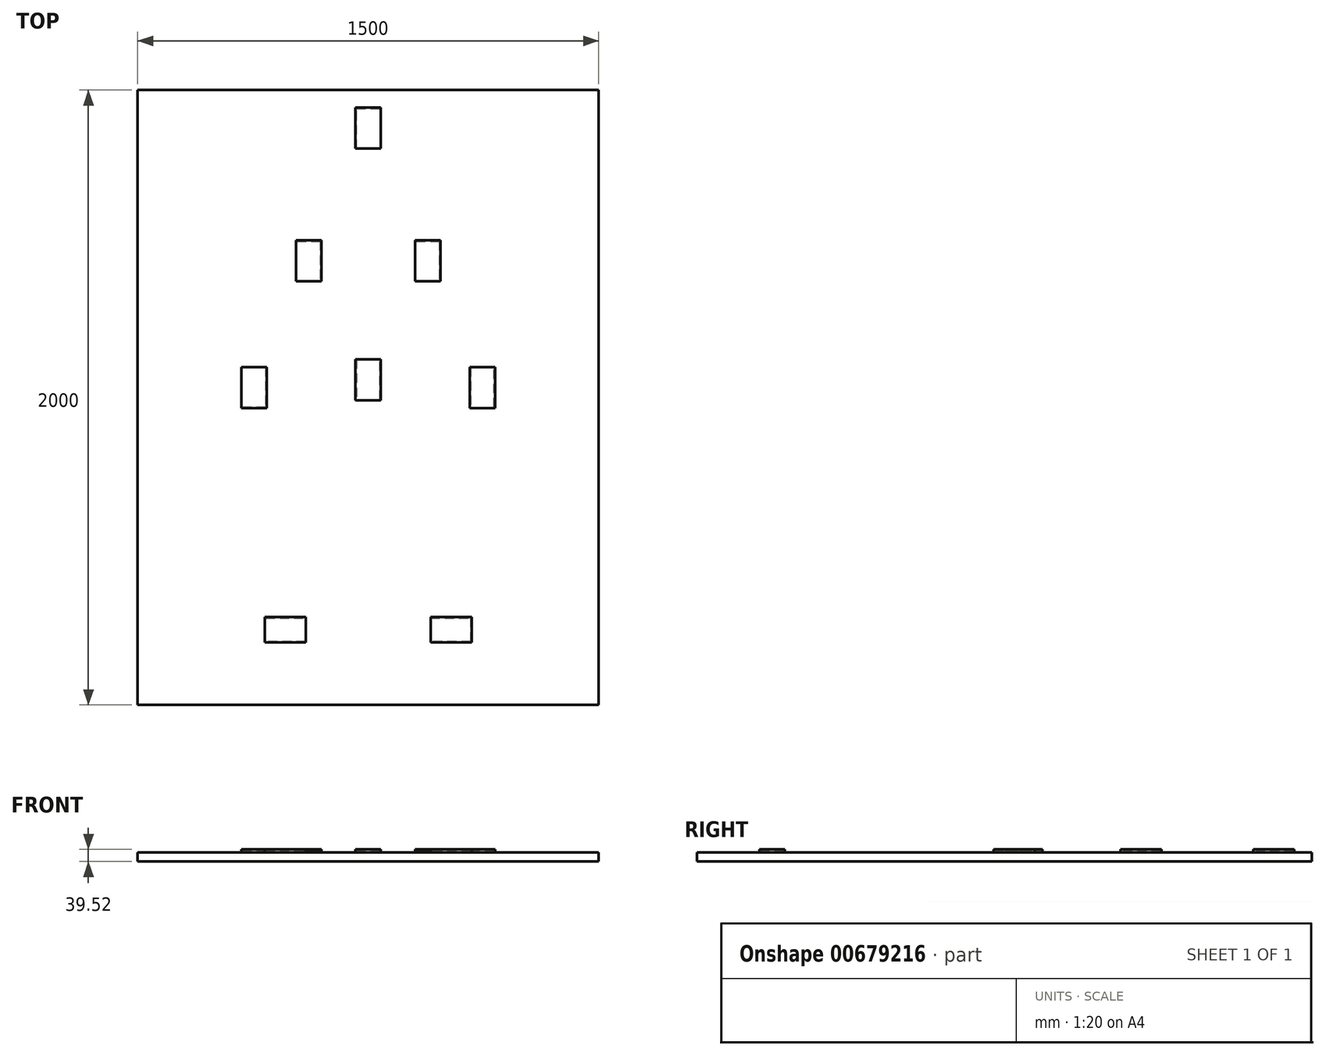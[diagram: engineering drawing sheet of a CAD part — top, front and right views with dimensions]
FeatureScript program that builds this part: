
annotation { "Feature Type Name" : "Feature", "Feature Type Description" : "" }
export const myFeature = defineFeature(function(context is Context, id is Id, definition is map)
    precondition{}
    {
        {
            var Q0;
            Q0=qCreatedBy(makeId("Top.planeOp"),FACE);
            var sketch = newSketch(context, id + "F0", { "sketchPlane" : qUnion([Q0])});
            skLineSegment(sketch, "E0.bottom", {"start": v(0, 0) * mm, "end": v(1500, 0) * mm});
            skLineSegment(sketch, "E0.top", {"start": v(0, 2000) * mm, "end": v(1500, 2000) * mm});
            skLineSegment(sketch, "E0.left", {"start": v(0, 0) * mm, "end": v(0, 2000) * mm});
            skLineSegment(sketch, "E0.right", {"start": v(1500, 0) * mm, "end": v(1500, 2000) * mm});
            skSolve(sketch);
        }
        {
            var Q0;
            Q0=makeQuery(id+"F0.imprint","IMPRINT",FACE,{"disambiguationData":[TD([[makeQuery(id+"F0.imprint","IMPRINT",EDGE,{"derivedFrom":sQuery(id+"F0.wireOp",EDGE,"E0.bottom")}),1.0]])]});
            extrude(context, id + "F1", {"entities" : qUnion([Q0]), "depth" : 5 * mm, "offsetDistance" : 25 * mm});
        }
        {
            var Q0;
            Q0=makeQuery(id+"F1.opExtrude","CAP_FACE",FACE,{"disambiguationData":[OSD([sQuery(id+"F0.wireOp",EDGE,"E0.bottom"),sQuery(id+"F0.wireOp",EDGE,"E0.top"),sQuery(id+"F0.wireOp",EDGE,"E0.left"),sQuery(id+"F0.wireOp",EDGE,"E0.right")])],"isStart":false});
            var sketch = newSketch(context, id + "F2", { "sketchPlane" : qUnion([Q0])});
            skLineSegment(sketch, "E1", {"start": v(0, 0) * mm, "end": v(10, 0) * mm});
            skLineSegment(sketch, "E2", {"start": v(10, 0) * mm, "end": v(10, 10) * mm});
            skLineSegment(sketch, "E3", {"start": v(1500, 2000) * mm, "end": v(1500, 1990) * mm});
            skLineSegment(sketch, "E4", {"start": v(1500, 1990) * mm, "end": v(1490, 1990) * mm});
            skLineSegment(sketch, "E5.bottom", {"start": v(1490, 1990) * mm, "end": v(10, 1990) * mm});
            skLineSegment(sketch, "E5.top", {"start": v(1490, 10) * mm, "end": v(10, 10) * mm});
            skLineSegment(sketch, "E5.left", {"start": v(1490, 1990) * mm, "end": v(1490, 10) * mm});
            skLineSegment(sketch, "E5.right", {"start": v(10, 1990) * mm, "end": v(10, 10) * mm});
            skSolve(sketch);
        }
        {
            var Q0;
            Q0=qSketchRegion(id+"F2",true);
            extrude(context, id + "F3", {"entities" : qUnion([Q0]), "depth" : 20 * mm, "offsetDistance" : 25 * mm});
        }
        {
            var Q0;
            Q0=makeQuery(id+"F2.imprint","IMPRINT",FACE,{"disambiguationData":[TD([[makeQuery(id+"F2.imprint","IMPRINT",EDGE,{"derivedFrom":sQuery(id+"F2.wireOp",EDGE,"E1")}),1.0]])]});
            var Q1;
            {var subQ1=sQuery(id+"F2.wireOp",EDGE,"E2");Q1=makeQuery(id+"F2.imprint","IMPRINT",FACE,{"disambiguationData":[TD([[makeQuery(id+"F2.imprint","IMPRINT",EDGE,{"derivedFrom":subQ1}),-1.0]])]});}
            extrude(context, id + "F4", {"entities" : qUnion([Q0, Q1]), "operationType" : NewBodyOperationType.ADD, "depth" : 20 * mm, "offsetDistance" : 25 * mm});
        }
        {
            var Q0;
            Q0=makeQuery(id+"F4.opExtrude","CAP_FACE",FACE,{"disambiguationData":[OSD([sQuery(id+"F0.wireOp",EDGE,"E0.bottom"),sQuery(id+"F0.wireOp",EDGE,"E0.top"),sQuery(id+"F0.wireOp",EDGE,"E0.left"),sQuery(id+"F0.wireOp",EDGE,"E0.right"),sQuery(id+"F2.wireOp",EDGE,"E1"),sQuery(id+"F2.wireOp",EDGE,"E3"),sQuery(id+"F2.wireOp",EDGE,"E5.bottom"),sQuery(id+"F2.wireOp",EDGE,"E5.top"),sQuery(id+"F2.wireOp",EDGE,"E5.left"),sQuery(id+"F2.wireOp",EDGE,"E5.right")])],"isStart":false});
            var sketch = newSketch(context, id + "F5", { "sketchPlane" : qUnion([Q0])});
            skLineSegment(sketch, "E6.bottom", {"start": v(0, 0) * mm, "end": v(1500, 0) * mm});
            skLineSegment(sketch, "E6.top", {"start": v(0, 2000) * mm, "end": v(1500, 2000) * mm});
            skLineSegment(sketch, "E6.left", {"start": v(0, 0) * mm, "end": v(0, 2000) * mm});
            skLineSegment(sketch, "E6.right", {"start": v(1500, 0) * mm, "end": v(1500, 2000) * mm});
            skSolve(sketch);
        }
        {
            var Q0;
            Q0=qSketchRegion(id+"F5",true);
            extrude(context, id + "F6", {"entities" : qUnion([Q0]), "operationType" : NewBodyOperationType.ADD, "depth" : 5 * mm, "offsetDistance" : 25 * mm});
        }
        {
            var Q0;
            Q0=makeQuery(id+"F6.opExtrude","CAP_FACE",FACE,{"disambiguationData":[OSD([sQuery(id+"F5.wireOp",EDGE,"E6.bottom"),sQuery(id+"F5.wireOp",EDGE,"E6.top"),sQuery(id+"F5.wireOp",EDGE,"E6.left"),sQuery(id+"F5.wireOp",EDGE,"E6.right")])],"isStart":false});
            var sketch = newSketch(context, id + "F7", { "sketchPlane" : qUnion([Q0])});
            skLineSegment(sketch, "E7", {"start": v(750, 0) * mm, "end": v(750, 203.2) * mm});
            skLineSegment(sketch, "E8", {"start": v(750, 203.2) * mm, "end": v(546.8, 203.2) * mm});
            skLineSegment(sketch, "E9", {"start": v(750, 203.2) * mm, "end": v(953.2, 203.2) * mm});
            skLineSegment(sketch, "E10", {"start": v(750, 203.2) * mm, "end": v(750, 990.6) * mm});
            skLineSegment(sketch, "E11", {"start": v(750, 990.6) * mm, "end": v(1080.2, 990.6) * mm});
            skLineSegment(sketch, "E12", {"start": v(750, 990.6) * mm, "end": v(419.8, 990.6) * mm});
            skLineSegment(sketch, "E13", {"start": v(419.8, 990.6) * mm, "end": v(419.8, 965.2) * mm});
            skLineSegment(sketch, "E14", {"start": v(1080.2, 990.6) * mm, "end": v(1080.2, 965.2) * mm});
            skLineSegment(sketch, "E15", {"start": v(750, 990.6) * mm, "end": v(750, 1377.95) * mm});
            skLineSegment(sketch, "E16", {"start": v(750, 1377.95) * mm, "end": v(902.4, 1377.95) * mm});
            skLineSegment(sketch, "E17", {"start": v(750, 1377.95) * mm, "end": v(597.6, 1377.95) * mm});
            skLineSegment(sketch, "E18", {"start": v(750, 1377.95) * mm, "end": v(750, 1809.75) * mm});
            skLineSegment(sketch, "E19.bottom", {"start": v(419.8, 965.2) * mm, "end": v(337.25, 965.2) * mm});
            skLineSegment(sketch, "E19.left", {"start": v(419.8, 965.2) * mm, "end": v(419.8, 1098.55) * mm});
            skLineSegment(sketch, "E19.right", {"start": v(337.25, 965.2) * mm, "end": v(337.25, 1098.55) * mm});
            skLineSegment(sketch, "E20.bottom", {"start": v(1080.2, 965.2) * mm, "end": v(1162.75, 965.2) * mm});
            skLineSegment(sketch, "E20.left", {"start": v(1080.2, 965.2) * mm, "end": v(1080.2, 1098.55) * mm});
            skLineSegment(sketch, "E20.right", {"start": v(1162.75, 965.2) * mm, "end": v(1162.75, 1098.55) * mm});
            skLineSegment(sketch, "E21.top", {"start": v(902.4, 1511.3) * mm, "end": v(984.95, 1511.3) * mm});
            skLineSegment(sketch, "E21.left", {"start": v(902.4, 1377.95) * mm, "end": v(902.4, 1511.3) * mm});
            skLineSegment(sketch, "E21.right", {"start": v(984.95, 1377.95) * mm, "end": v(984.95, 1511.3) * mm});
            skLineSegment(sketch, "E22.top", {"start": v(597.6, 1511.3) * mm, "end": v(515.05, 1511.3) * mm});
            skLineSegment(sketch, "E22.left", {"start": v(597.6, 1377.95) * mm, "end": v(597.6, 1511.3) * mm});
            skLineSegment(sketch, "E22.right", {"start": v(515.05, 1377.95) * mm, "end": v(515.05, 1511.3) * mm});
            skLineSegment(sketch, "E23", {"start": v(750, 1809.75) * mm, "end": v(708.73, 1809.75) * mm});
            skLineSegment(sketch, "E24.top", {"start": v(708.73, 1943.1) * mm, "end": v(791.28, 1943.1) * mm});
            skLineSegment(sketch, "E24.left", {"start": v(708.73, 1809.75) * mm, "end": v(708.73, 1943.1) * mm});
            skLineSegment(sketch, "E24.right", {"start": v(791.28, 1809.75) * mm, "end": v(791.28, 1943.1) * mm});
            skLineSegment(sketch, "E25.bottom", {"start": v(953.2, 203.2) * mm, "end": v(1086.55, 203.2) * mm});
            skLineSegment(sketch, "E25.top", {"start": v(953.2, 285.75) * mm, "end": v(1086.55, 285.75) * mm});
            skLineSegment(sketch, "E25.right", {"start": v(1086.55, 203.2) * mm, "end": v(1086.55, 285.75) * mm});
            skLineSegment(sketch, "E26.bottom", {"start": v(546.8, 203.2) * mm, "end": v(413.45, 203.2) * mm});
            skLineSegment(sketch, "E26.top", {"start": v(546.8, 285.75) * mm, "end": v(413.45, 285.75) * mm});
            skLineSegment(sketch, "E26.right", {"start": v(413.45, 203.2) * mm, "end": v(413.45, 285.75) * mm});
            skLineSegment(sketch, "E27", {"start": v(515.05, 1377.95) * mm, "end": v(518.23, 1377.95) * mm});
            skLineSegment(sketch, "E28", {"start": v(518.23, 1377.95) * mm, "end": v(518.23, 1508.13) * mm});
            skLineSegment(sketch, "E29", {"start": v(518.23, 1508.13) * mm, "end": v(594.43, 1508.13) * mm});
            skLineSegment(sketch, "E30", {"start": v(594.43, 1508.13) * mm, "end": v(594.43, 1377.95) * mm});
            skLineSegment(sketch, "E31", {"start": v(594.43, 1377.95) * mm, "end": v(597.6, 1377.95) * mm});
            skLineSegment(sketch, "E32", {"start": v(902.4, 1377.95) * mm, "end": v(905.58, 1377.95) * mm});
            skLineSegment(sketch, "E33", {"start": v(905.58, 1377.95) * mm, "end": v(905.58, 1508.13) * mm});
            skLineSegment(sketch, "E34", {"start": v(905.58, 1508.13) * mm, "end": v(981.78, 1508.13) * mm});
            skLineSegment(sketch, "E35", {"start": v(981.78, 1508.13) * mm, "end": v(981.78, 1377.95) * mm});
            skLineSegment(sketch, "E36", {"start": v(981.78, 1377.95) * mm, "end": v(984.95, 1377.95) * mm});
            skLineSegment(sketch, "E37", {"start": v(708.73, 1809.75) * mm, "end": v(711.9, 1809.75) * mm});
            skLineSegment(sketch, "E38", {"start": v(711.9, 1809.75) * mm, "end": v(711.9, 1939.93) * mm});
            skLineSegment(sketch, "E39", {"start": v(711.9, 1939.93) * mm, "end": v(788.1, 1939.93) * mm});
            skLineSegment(sketch, "E40", {"start": v(788.1, 1939.93) * mm, "end": v(788.1, 1809.75) * mm});
            skLineSegment(sketch, "E41", {"start": v(788.1, 1809.75) * mm, "end": v(791.28, 1809.75) * mm});
            skLineSegment(sketch, "E42", {"start": v(419.8, 1098.55) * mm, "end": v(416.62, 1098.55) * mm});
            skLineSegment(sketch, "E43", {"start": v(416.62, 1098.55) * mm, "end": v(416.62, 968.38) * mm});
            skLineSegment(sketch, "E44", {"start": v(416.62, 968.38) * mm, "end": v(340.42, 968.38) * mm});
            skLineSegment(sketch, "E45", {"start": v(340.42, 968.38) * mm, "end": v(340.42, 1098.55) * mm});
            skLineSegment(sketch, "E46", {"start": v(340.42, 1098.55) * mm, "end": v(337.25, 1098.55) * mm});
            skLineSegment(sketch, "E47", {"start": v(1080.2, 1098.55) * mm, "end": v(1083.38, 1098.55) * mm});
            skLineSegment(sketch, "E48", {"start": v(1083.38, 1098.55) * mm, "end": v(1083.38, 968.38) * mm});
            skLineSegment(sketch, "E49", {"start": v(1083.38, 968.38) * mm, "end": v(1159.58, 968.38) * mm});
            skLineSegment(sketch, "E50", {"start": v(1159.58, 968.38) * mm, "end": v(1159.58, 1098.55) * mm});
            skLineSegment(sketch, "E51", {"start": v(1159.58, 1098.55) * mm, "end": v(1162.75, 1098.55) * mm});
            skLineSegment(sketch, "E52", {"start": v(546.8, 203.2) * mm, "end": v(546.8, 206.38) * mm});
            skLineSegment(sketch, "E53", {"start": v(546.8, 206.38) * mm, "end": v(416.62, 206.38) * mm});
            skLineSegment(sketch, "E54", {"start": v(416.62, 206.38) * mm, "end": v(416.62, 282.58) * mm});
            skLineSegment(sketch, "E55", {"start": v(416.62, 282.58) * mm, "end": v(546.8, 282.58) * mm});
            skLineSegment(sketch, "E56", {"start": v(546.8, 282.58) * mm, "end": v(546.8, 285.75) * mm});
            skLineSegment(sketch, "E57", {"start": v(953.2, 285.75) * mm, "end": v(953.2, 282.58) * mm});
            skLineSegment(sketch, "E58", {"start": v(953.2, 282.58) * mm, "end": v(1083.38, 282.58) * mm});
            skLineSegment(sketch, "E59", {"start": v(1083.38, 282.58) * mm, "end": v(1083.38, 206.38) * mm});
            skLineSegment(sketch, "E60", {"start": v(1083.38, 206.38) * mm, "end": v(953.2, 206.38) * mm});
            skLineSegment(sketch, "E61", {"start": v(953.2, 206.38) * mm, "end": v(953.2, 203.2) * mm});
            skLineSegment(sketch, "E62", {"start": v(1162.75, 1098.55) * mm, "end": v(1080.2, 1098.55) * mm});
            skLineSegment(sketch, "E63", {"start": v(984.95, 1377.95) * mm, "end": v(902.4, 1377.95) * mm});
            skLineSegment(sketch, "E64", {"start": v(597.6, 1377.95) * mm, "end": v(515.05, 1377.95) * mm});
            skLineSegment(sketch, "E65", {"start": v(419.8, 1098.55) * mm, "end": v(337.25, 1098.55) * mm});
            skLineSegment(sketch, "E66", {"start": v(791.28, 1809.75) * mm, "end": v(708.73, 1809.75) * mm});
            skLineSegment(sketch, "E67", {"start": v(953.2, 203.2) * mm, "end": v(953.2, 285.75) * mm});
            skLineSegment(sketch, "E68", {"start": v(546.8, 203.2) * mm, "end": v(546.8, 285.75) * mm});
            skLineSegment(sketch, "E69", {"start": v(750, 990.6) * mm, "end": v(708.73, 990.6) * mm});
            skLineSegment(sketch, "E70.bottom", {"start": v(708.73, 990.6) * mm, "end": v(791.28, 990.6) * mm});
            skLineSegment(sketch, "E70.top", {"start": v(708.73, 1123.95) * mm, "end": v(791.28, 1123.95) * mm});
            skLineSegment(sketch, "E70.left", {"start": v(708.73, 990.6) * mm, "end": v(708.73, 1123.95) * mm});
            skLineSegment(sketch, "E70.right", {"start": v(791.28, 990.6) * mm, "end": v(791.28, 1123.95) * mm});
            skLineSegment(sketch, "E71", {"start": v(708.73, 1123.95) * mm, "end": v(711.9, 1123.95) * mm});
            skLineSegment(sketch, "E72", {"start": v(711.9, 1123.95) * mm, "end": v(711.9, 993.78) * mm});
            skLineSegment(sketch, "E73", {"start": v(711.9, 993.78) * mm, "end": v(788.1, 993.78) * mm});
            skLineSegment(sketch, "E74", {"start": v(788.1, 993.78) * mm, "end": v(788.1, 1123.95) * mm});
            skSolve(sketch);
        }
        {
            var Q0;
            Q0=makeQuery(id+"F7.imprint","IMPRINT",FACE,{"disambiguationData":[TD([[makeQuery(id+"F7.imprint","IMPRINT",EDGE,{"derivedFrom":sQuery(id+"F7.wireOp",EDGE,"E22.top")}),1.0]])]});
            var Q1;
            {var subQ0=sQuery(id+"F7.wireOp",EDGE,"E28");Q1=makeQuery(id+"F7.imprint","IMPRINT",FACE,{"disambiguationData":[TD([[makeQuery(id+"F7.imprint","IMPRINT",EDGE,{"derivedFrom":subQ0}),-1.0]])]});}
            var Q2;
            {var subQ0=sQuery(id+"F7.wireOp",EDGE,"E33");Q2=makeQuery(id+"F7.imprint","IMPRINT",FACE,{"disambiguationData":[TD([[makeQuery(id+"F7.imprint","IMPRINT",EDGE,{"derivedFrom":subQ0}),-1.0]])]});}
            var Q3;
            Q3=makeQuery(id+"F7.imprint","IMPRINT",FACE,{"disambiguationData":[TD([[makeQuery(id+"F7.imprint","IMPRINT",EDGE,{"derivedFrom":sQuery(id+"F7.wireOp",EDGE,"E21.top")}),-1.0]])]});
            var Q4;
            Q4=makeQuery(id+"F7.imprint","IMPRINT",FACE,{"disambiguationData":[TD([[makeQuery(id+"F7.imprint","IMPRINT",EDGE,{"derivedFrom":sQuery(id+"F7.wireOp",EDGE,"E24.top")}),-1.0]])]});
            var Q5;
            {var subQ3=sQuery(id+"F7.wireOp",EDGE,"E38");Q5=makeQuery(id+"F7.imprint","IMPRINT",FACE,{"disambiguationData":[TD([[makeQuery(id+"F7.imprint","IMPRINT",EDGE,{"derivedFrom":subQ3}),-1.0]])]});}
            var Q6;
            {var subQ5=sQuery(id+"F7.wireOp",EDGE,"E19.bottom");Q6=makeQuery(id+"F7.imprint","IMPRINT",FACE,{"disambiguationData":[TD([[makeQuery(id+"F7.imprint","IMPRINT",EDGE,{"derivedFrom":subQ5}),-1.0]])]});}
            var Q7;
            {var subQ0=sQuery(id+"F7.wireOp",EDGE,"E43");Q7=makeQuery(id+"F7.imprint","IMPRINT",FACE,{"disambiguationData":[TD([[makeQuery(id+"F7.imprint","IMPRINT",EDGE,{"derivedFrom":subQ0}),-1.0]])]});}
            var Q8;
            {var subQ0=sQuery(id+"F7.wireOp",EDGE,"E53");Q8=makeQuery(id+"F7.imprint","IMPRINT",FACE,{"disambiguationData":[TD([[makeQuery(id+"F7.imprint","IMPRINT",EDGE,{"derivedFrom":subQ0}),-1.0]])]});}
            var Q9;
            {var subQ4=sQuery(id+"F7.wireOp",EDGE,"E26.bottom");Q9=makeQuery(id+"F7.imprint","IMPRINT",FACE,{"disambiguationData":[TD([[makeQuery(id+"F7.imprint","IMPRINT",EDGE,{"derivedFrom":subQ4}),-1.0]])]});}
            var Q10;
            {var subQ0=sQuery(id+"F7.wireOp",EDGE,"E58");Q10=makeQuery(id+"F7.imprint","IMPRINT",FACE,{"disambiguationData":[TD([[makeQuery(id+"F7.imprint","IMPRINT",EDGE,{"derivedFrom":subQ0}),-1.0]])]});}
            var Q11;
            {var subQ3=sQuery(id+"F7.wireOp",EDGE,"E25.bottom");Q11=makeQuery(id+"F7.imprint","IMPRINT",FACE,{"disambiguationData":[TD([[makeQuery(id+"F7.imprint","IMPRINT",EDGE,{"derivedFrom":subQ3}),1.0]])]});}
            var Q12;
            {var subQ5=sQuery(id+"F7.wireOp",EDGE,"E20.bottom");Q12=makeQuery(id+"F7.imprint","IMPRINT",FACE,{"disambiguationData":[TD([[makeQuery(id+"F7.imprint","IMPRINT",EDGE,{"derivedFrom":subQ5}),1.0]])]});}
            var Q13;
            {var subQ0=sQuery(id+"F7.wireOp",EDGE,"E48");Q13=makeQuery(id+"F7.imprint","IMPRINT",FACE,{"disambiguationData":[TD([[makeQuery(id+"F7.imprint","IMPRINT",EDGE,{"derivedFrom":subQ0}),1.0]])]});}
            var Q14;
            {var subQ5=sQuery(id+"F7.wireOp",EDGE,"E72");Q14=makeQuery(id+"F7.imprint","IMPRINT",FACE,{"disambiguationData":[TD([[makeQuery(id+"F7.imprint","IMPRINT",EDGE,{"derivedFrom":subQ5}),1.0]])]});}
            var Q15;
            {var subQ0=sQuery(id+"F7.wireOp",EDGE,"E70.left");Q15=makeQuery(id+"F7.imprint","IMPRINT",FACE,{"disambiguationData":[TD([[makeQuery(id+"F7.imprint","IMPRINT",EDGE,{"derivedFrom":subQ0}),-1.0]])]});}
            var Q16;
            {var subQ0=sQuery(id+"F7.wireOp",EDGE,"E70.right");Q16=makeQuery(id+"F7.imprint","IMPRINT",FACE,{"disambiguationData":[TD([[makeQuery(id+"F7.imprint","IMPRINT",EDGE,{"derivedFrom":subQ0}),1.0]])]});}
            var Q17;
            {var subQ5=sQuery(id+"F7.wireOp",EDGE,"E74");Q17=makeQuery(id+"F7.imprint","IMPRINT",FACE,{"disambiguationData":[TD([[makeQuery(id+"F7.imprint","IMPRINT",EDGE,{"derivedFrom":subQ5}),1.0]])]});}
            extrude(context, id + "F8", {"entities" : qUnion([Q0, Q1, Q2, Q3, Q4, Q5, Q6, Q7, Q8, Q9, Q10, Q11, Q12, Q13, Q14, Q15, Q16, Q17]), "depth" : 9.52 * mm, "offsetDistance" : 25.4 * mm});
        }
        {
            var Q0;
            {var subQ0=sQuery(id+"F7.wireOp",EDGE,"E28");Q0=makeQuery(id+"F7.imprint","IMPRINT",FACE,{"disambiguationData":[TD([[makeQuery(id+"F7.imprint","IMPRINT",EDGE,{"derivedFrom":subQ0}),-1.0]])]});}
            var Q1;
            {var subQ0=sQuery(id+"F7.wireOp",EDGE,"E33");Q1=makeQuery(id+"F7.imprint","IMPRINT",FACE,{"disambiguationData":[TD([[makeQuery(id+"F7.imprint","IMPRINT",EDGE,{"derivedFrom":subQ0}),-1.0]])]});}
            var Q2;
            {var subQ3=sQuery(id+"F7.wireOp",EDGE,"E38");Q2=makeQuery(id+"F7.imprint","IMPRINT",FACE,{"disambiguationData":[TD([[makeQuery(id+"F7.imprint","IMPRINT",EDGE,{"derivedFrom":subQ3}),-1.0]])]});}
            var Q3;
            {var subQ0=sQuery(id+"F7.wireOp",EDGE,"E43");Q3=makeQuery(id+"F7.imprint","IMPRINT",FACE,{"disambiguationData":[TD([[makeQuery(id+"F7.imprint","IMPRINT",EDGE,{"derivedFrom":subQ0}),-1.0]])]});}
            var Q4;
            {var subQ0=sQuery(id+"F7.wireOp",EDGE,"E48");Q4=makeQuery(id+"F7.imprint","IMPRINT",FACE,{"disambiguationData":[TD([[makeQuery(id+"F7.imprint","IMPRINT",EDGE,{"derivedFrom":subQ0}),1.0]])]});}
            var Q5;
            {var subQ0=sQuery(id+"F7.wireOp",EDGE,"E58");Q5=makeQuery(id+"F7.imprint","IMPRINT",FACE,{"disambiguationData":[TD([[makeQuery(id+"F7.imprint","IMPRINT",EDGE,{"derivedFrom":subQ0}),-1.0]])]});}
            var Q6;
            {var subQ0=sQuery(id+"F7.wireOp",EDGE,"E53");Q6=makeQuery(id+"F7.imprint","IMPRINT",FACE,{"disambiguationData":[TD([[makeQuery(id+"F7.imprint","IMPRINT",EDGE,{"derivedFrom":subQ0}),-1.0]])]});}
            var Q7;
            {var subQ5=sQuery(id+"F7.wireOp",EDGE,"E72");Q7=makeQuery(id+"F7.imprint","IMPRINT",FACE,{"disambiguationData":[TD([[makeQuery(id+"F7.imprint","IMPRINT",EDGE,{"derivedFrom":subQ5}),1.0]])]});}
            var Q8;
            {var subQ5=sQuery(id+"F7.wireOp",EDGE,"E74");Q8=makeQuery(id+"F7.imprint","IMPRINT",FACE,{"disambiguationData":[TD([[makeQuery(id+"F7.imprint","IMPRINT",EDGE,{"derivedFrom":subQ5}),1.0]])]});}
            extrude(context, id + "F9", {"entities" : qUnion([Q0, Q1, Q2, Q3, Q4, Q5, Q6, Q7, Q8]), "operationType" : NewBodyOperationType.REMOVE, "depth" : 6.35 * mm, "offsetDistance" : 25.4 * mm});
        }
    });
